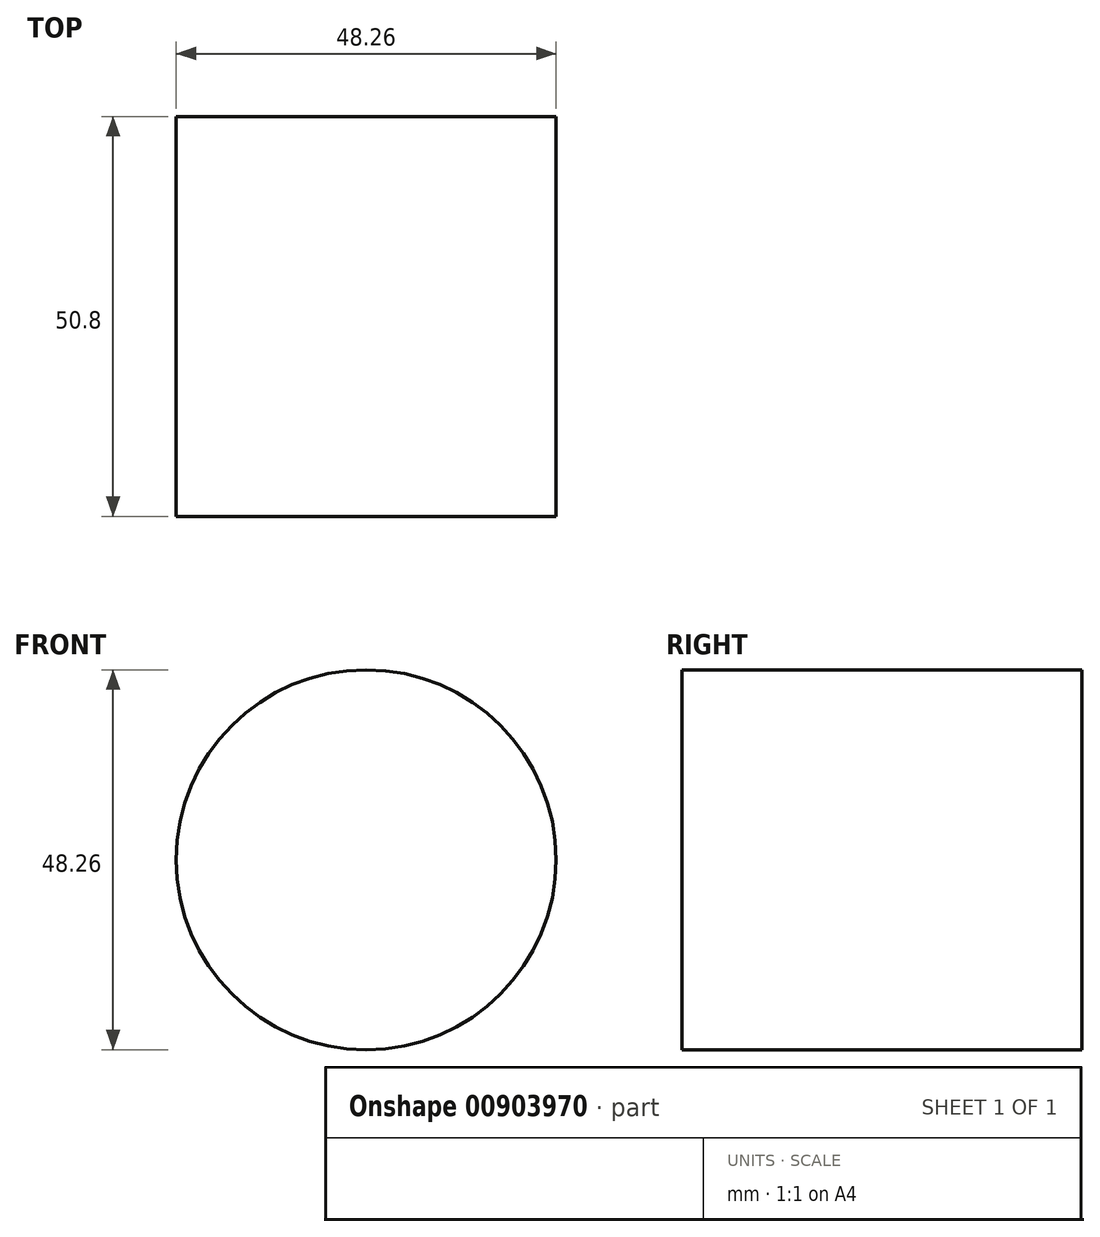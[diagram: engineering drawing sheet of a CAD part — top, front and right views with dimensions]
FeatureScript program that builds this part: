
annotation { "Feature Type Name" : "Feature", "Feature Type Description" : "" }
export const myFeature = defineFeature(function(context is Context, id is Id, definition is map)
    precondition{}
    {
        {
            var Q0;
            Q0=qCreatedBy(makeId("Front.planeOp"),FACE);
            var sketch = newSketch(context, id + "F0", { "sketchPlane" : qUnion([Q0])});
            skCircle(sketch, "E0", {"center": v(0, 0) * mm, "radius": 24.13 * mm});
            skSolve(sketch);
        }
        {
            var Q0;
            Q0 = qSketchRegion(id + "F0", true);
            extrude(context, id + "F1", {"entities" : qUnion([Q0]), "depth" : 50.8 * mm, "offsetDistance" : 25.4 * mm});
        }
    });
